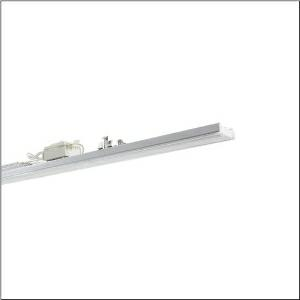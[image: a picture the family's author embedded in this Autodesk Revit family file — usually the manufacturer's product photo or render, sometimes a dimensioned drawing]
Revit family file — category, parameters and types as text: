
# Revit family: licross_r__11_recessed_ho_51tl1wmv465m_7aaa
name_source: partatom
category: Lighting Fixtures
units: mm (PartAtom-declared; Revit-internal decimal feet)

## family parameters
Cut with Voids When Loaded = No
Host = Face
Light Source = No
Part Type = Normal
Room Calculation Point = No
Round Connector Dimension = Use Diameter
Shared = No

## types (1)
- --- (1 x LED, 6760 lm, 32.3 W, 4000K)
    Apparent Load = 32 VA
    CIE Flux Codes = 73 94 99 100 100
    Color Rendering = 80
    Color Temperature = 4000K
    Default Elevation = 1800 mm
    Description = Licross® 11 Recessed HO, luminaire insert, of sheet steel, coil coated, white, length: 2.250mm, width: 66mm, height: 67mm, LED rated luminous flux: 6.760lm, light colour: 840, control gear: ON/OFF Multilumen, with plug, 3-pole, with phase selection, mains connection: 220..240V, AC, 50/60Hz, rated input power: 32W, internal wiring halogen-free, primary optical cover: cover, of PMMA, light emission: direct distribution, primary light characteristic: symmetric, protection rating (complete): IP40, insulation class (complete): insulation class I (protective earthing), certification: CE, ENEC, VDE, UKCA, protection symbol: D if used in an environment without relevant dust loads with corresponding accessories, impact resistance: IK06, permissible ambient temperature for indoor applications: -35..+50°C, corresponds to IFS (International Featured Standards) requirements for safety and quality in the food industry, reducing of maximum allowable ambient temperature of 5°C with ceiling mounting, packaging unit: 1 piece
    Height = 58 mm
    Lamp = 1 x LED
    Lamp Light Flux = 6760 lm
    Lamp Power = 32.3 W
    Lamp count = 1
    Length = 2250 mm
    Luminous efficacy = 209 lm/W
    Manufacturer = Siteco
    ModVariant = No
    Model = 51TL1WMV465M
    Mounting Place = Ceiling
    Mounting Type = Pendant
    Number of Poles = 1
    OnlyDefault = Yes
    Power Factor = 1
    Product Name = Licross® 11 Recessed HO
    Product group = luminaire insert | ceiling pendant
    ProductGroupID = 902
    Protection Class = Protection class I
    Protection Degree = IP 40
    RLX_Detail_Level = 1
    RLX_Emergency_Light_Flux = 0 lm
    RLX_Emergency_Type = 0
    RLX_Emergency_Type_DB = No
    RlxData = <blob elided: 26993 chars, md5=1f0741bf>
    Socket = socket
    Standby Power = 0 W
    System Light Flux = 6760 lm
    System Power = 32 W
    Type Comments = factory setting: luminous flux: 100 % | (A | C | E) | 77 mA
    Type Image = l_1296930.jpg
    URL = http://relux.com
    VarID = @adj_061733
    Voltage = 0 V
    Weight = 0.00 kg
    Width = 66 mm

## geometry (parser evidence)
native form markers: Blend x4, Sweep x12
no freeform markers — native parametric forms only
